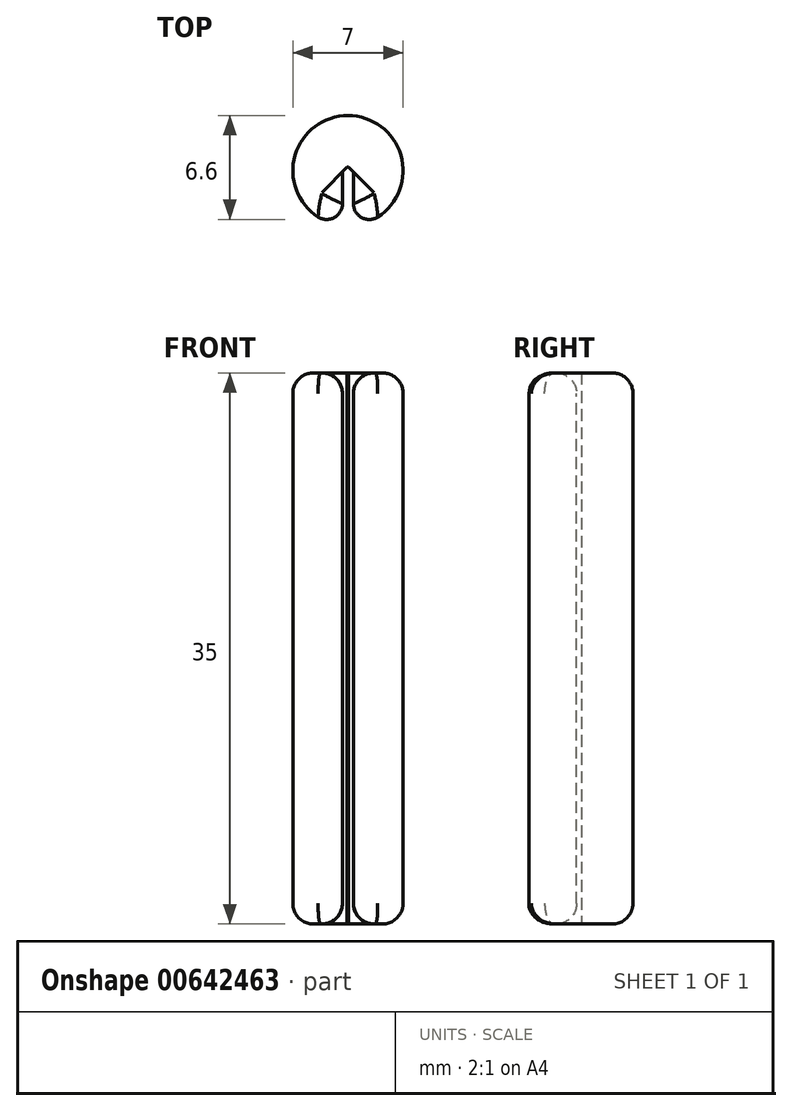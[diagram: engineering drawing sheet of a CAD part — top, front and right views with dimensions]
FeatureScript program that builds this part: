
annotation { "Feature Type Name" : "Feature", "Feature Type Description" : "" }
export const myFeature = defineFeature(function(context is Context, id is Id, definition is map)
    precondition{}
    {
        {
            var Q0;
            Q0=qCreatedBy(makeId("Top.planeOp"),FACE);
            var sketch = newSketch(context, id + "F0", { "sketchPlane" : qUnion([Q0])});
            skArc(sketch, "E0", {"start": v(0.35, -3.48) * mm, "mid": v(0, 3.5) * mm, "end": v(-0.35, -3.48) * mm});
            skLineSegment(sketch, "E1.bottom", {"start": v(-0.35, 0.22) * mm, "end": v(0.35, 0.22) * mm});
            skLineSegment(sketch, "E1.left", {"start": v(-0.35, 0.22) * mm, "end": v(-0.35, -3.48) * mm});
            skLineSegment(sketch, "E1.right", {"start": v(0.35, 0.22) * mm, "end": v(0.35, -3.48) * mm});
            skPoint(sketch, "E1.middle", {"position": v(0, -5.78) * mm});
            skPoint(sketch, "E1.top.end.orphan", {"position": v(0.35, -11.78) * mm});
            skPoint(sketch, "E1.top.start.orphan", {"position": v(-0.35, -11.78) * mm});
            skSolve(sketch);
        }
        {
            var Q0;
            Q0 = qSketchRegion(id + "F0", true);
            extrude(context, id + "F1", {"entities" : qUnion([Q0]), "depth" : 35 * mm, "offsetDistance" : 25 * mm});
        }
        {
            var Q0;
            Q0=makeQuery(id+"F1.opExtrude","SWEPT_EDGE",EDGE,{"disambiguationData":[OSD([sQuery(id+"F0.wireOp",EDGE,"E0"),sQuery(id+"F0.wireOp",EDGE,"E1.right")])]});
            var Q1;
            Q1=makeQuery(id+"F1.opExtrude","SWEPT_EDGE",EDGE,{"disambiguationData":[OSD([sQuery(id+"F0.wireOp",EDGE,"E0"),sQuery(id+"F0.wireOp",EDGE,"E1.left")])]});
            fillet(context, id + "F2", {"entities" : qUnion([Q0, Q1]), "radius" : 1 * mm, "tangentPropagation" : true, "allowEdgeOverflow" : false});
        }
        {
            var Q0;
            Q0=makeQuery(id+"F1.opExtrude","SWEPT_EDGE",EDGE,{"disambiguationData":[OSD([sQuery(id+"F0.wireOp",EDGE,"E1.bottom"),sQuery(id+"F0.wireOp",EDGE,"E1.left")])]});
            var Q1;
            Q1=makeQuery(id+"F1.opExtrude","SWEPT_EDGE",EDGE,{"disambiguationData":[OSD([sQuery(id+"F0.wireOp",EDGE,"E1.bottom"),sQuery(id+"F0.wireOp",EDGE,"E1.right")])]});
            chamfer(context, id + "F3", {"entities" : qUnion([Q0, Q1]), "width" : .3 * mm, "tangentPropagation" : true});
        }
        {
            var Q0;
            Q0=makeQuery(id+"F1.opExtrude","CAP_EDGE",EDGE,{"disambiguationData":[OSD([sQuery(id+"F0.wireOp",EDGE,"E0")])],"isStart":true});
            var Q1;
            Q1=makeQuery(id+"F1.opExtrude","CAP_EDGE",EDGE,{"disambiguationData":[OSD([sQuery(id+"F0.wireOp",EDGE,"E0")])],"isStart":false});
            fillet(context, id + "F4", {"entities" : qUnion([Q0, Q1]), "radius" : 1.3 * mm, "tangentPropagation" : true, "allowEdgeOverflow" : false});
        }
    });
